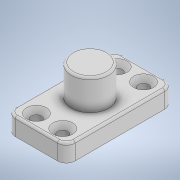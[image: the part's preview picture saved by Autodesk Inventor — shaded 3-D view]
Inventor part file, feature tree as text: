
AUTODESK INVENTOR PART (.ipt)
format: ipt  version: 2020.3 (Build 243373000, 373)  size: 177,152 bytes
history: native  units: mm
features: extrude x3, sketch x2, fillet x2, hole x1
ambient origin geometry x8: Origin, YZ Plane, XZ Plane, XY Plane, X Axis, Y Axis, Z Axis, Center Point
bodies: Solid1 (feature_tree)
feature tree (8):
  sketch  "Sketch1"  dims[d0=24.6mm d1=12.4mm]
  extrude  "Extrusion1"  Depth=12.4mm
  extrude  "Extrusion2"  Depth=2.0mm
  fillet  "Fillet1"  Radius=4.0mm
  extrude  "Extrusion3"  Depth=4.0mm TaperAngle=0.0deg
  fillet  "Fillet2"  Radius=2.0mm
  hole  "Hole2"  [1 undecoded]
  sketch  "Sketch3"  dims[d2=6.0mm d4=6.0mm d5=4.0mm d6=0.0mm d7=4.0mm d8=0.0mm d16=2.0mm d17=8.5mm d18=11.0mm d19=0.0mm d20=0.5mm d21=6.8mm d28=2.3mm d29=6.0mm d30=4.5mm d31=2.0mm d32=90.0deg d33=6.5mm d34=0.0mm]
note: 1 required parameter value undecoded (feature->parameter linkage not recoverable at this tier; creation-order binding heuristic only, values carry confidence <= 0.55)
